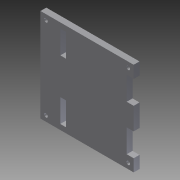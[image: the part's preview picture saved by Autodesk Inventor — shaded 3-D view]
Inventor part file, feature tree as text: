
AUTODESK INVENTOR PART (.ipt)
format: ipt  version: 2011 (Build 150239000, 239)  size: 332,288 bytes
history: native  units: in
note: dims shown in document units (in); Inventor stores cm internally (conversion verified against a paired STEP export)
features: extrude x15, sketch x15
ambient origin geometry x8: Origin, YZ Plane, XZ Plane, XY Plane, X Axis, Y Axis, Z Axis, Center Point
bodies: Solid1 (feature_tree)
feature tree (30):
  extrude  "Extrusion1"  Depth=4.05in
  extrude  "Extrusion2"  Depth=2.05in
  extrude  "Extrusion3"  Depth=1.7in
  extrude  "Extrusion4"  Depth=1.0in
  extrude  "Extrusion5"  Depth=1.75in
  extrude  "Extrusion6"  Depth=1.0in
  extrude  "Extrusion7"  Depth=1.0in
  extrude  "Extrusion8"  Depth=1.0in
  extrude  "Extrusion9"  Depth=1.0in
  extrude  "Extrusion10"  Depth=1.0in
  extrude  "Extrusion11"  Depth=1.0in
  extrude  "Extrusion12"  Depth=0.2345in
  extrude  "Extrusion13"  Depth=0.2345in
  extrude  "Extrusion14"  Depth=4.0in
  extrude  "Extrusion15"  Depth=0.156in
  sketch  "Sketch1"  dims[d0=4.0in d1=4.05in]
  sketch  "Sketch2"  dims[d2=2.0in d3=2.05in]
  sketch  "Sketch3"  dims[d4=0.9in d5=1.7in]
  sketch  "Sketch4"  dims[d6=1.8in d7=1.0in]
  sketch  "Sketch5"  dims[d8=0.3in d9=1.75in]
  sketch  "Sketch6"  dims[d10=0.25in d11=1.0in]
  sketch  "Sketch7"  dims[d12=0.25in d13=1.0in]
  sketch  "Sketch8"  dims[d14=1.275in d15=1.0in]
  sketch  "Sketch9"  dims[d16=0.25in d17=1.0in]
  sketch  "Sketch11"  dims[d18=0.275in d19=1.0in]
  sketch  "Sketch12"  dims[d20=0.25in d21=0.0in d22=1.0in]
  sketch  "Sketch13"  dims[d23=0.25in d24=0.0in d25=0.2345in]
  sketch  "Sketch14"  dims[d26=0.2345in d27=0.2345in]
  sketch  "Sketch15"  dims[d28=0.2345in d29=4.0in]
  sketch  "Sketch16"  dims[d30=0.156in d31=0.156in d32=0.25in d33=0.0in d34=0.5in d35=0.5in d36=0.25in d37=0.0in d38=4.0in d39=0.2345in d40=0.2345in d41=4.0in d42=0.5in d43=0.3in d44=0.2in d45=0.25in d46=0.0in d47=0.3in d48=0.25in d49=0.0in d50=4.0in d51=0.2345in d52=4.0in d53=0.2345in d54=0.2345in d55=0.2345in d56=0.156in d57=0.156in d58=0.25in d59=0.0in d60=4.0in d61=0.25in d62=0.0in d63=0.25in d64=0.0in d67=1.0in d68=1.0in d69=0.3in d70=0.25in d71=0.0in d72=0.25in d73=0.0in d74=0.25in d75=0.0in d76=0.25in d77=0.0in d78=0.025in d79=0.025in d80=0.25in d81=0.0in d82=2.0in d83=1.7655in d84=0.156in d85=0.156in d86=0.156in d87=0.156in d88=0.25in d89=0.0in]
